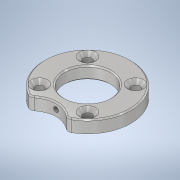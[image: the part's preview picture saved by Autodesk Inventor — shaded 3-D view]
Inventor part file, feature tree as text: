
AUTODESK INVENTOR PART (.ipt)
format: ipt  version: 2020.1 (Build 241239000, 239)  size: 221,696 bytes
history: native  units: mm
features: chamfer x3, fillet x2, sketch x2, projected_geometry x2, extrude x1, plane x1, hole x1, thread x1
ambient origin geometry x8: Origin, YZ Plane, XZ Plane, XY Plane, X Axis, Y Axis, Z Axis, Center Point
bodies: Solid1 (feature_tree)
feature tree (13):
  extrude  "Extrusion1"  Depth=3.5mm
  fillet  "Fillet1"  Radius=40.0mm
  fillet  "Fillet2"  [1 undecoded]
  chamfer  "Chamfer1"  Distance=15.0mm
  chamfer  "Chamfer2"  Distance=5.0mm
  chamfer  "Chamfer3"  Distance=2.0mm
  plane  "Work Plane1"
  hole  "Hole1"  [1 undecoded]
  thread  "Thread5"  [1 undecoded]
  sketch  "Sketch1"  dims[d0=18.5mm d2=3.5mm d4=40.0mm d6=360.0deg d8=45.0deg]
  sketch  "Sketch2"  dims[d10=19.0mm d11=15.0mm d12=5.0mm d13=0.0mm d14=2.0mm d15=1.0mm d24=0.5mm d25=2.0mm d26=45.0deg d27=0.0mm d30=8.0mm d32=0.5mm d33=2.0mm d34=45.0deg d36=27.5mm d37=1.5mm d38=2.0mm d39=45.0deg d40=2.5mm d41=5.0mm d42=2.5mm d43=2.0mm d44=6.0mm d45=4.0mm d46=2.0mm d47=90.0deg d48=8.0mm d49=0.0mm d50=3.516mm d51=0.0mm d52=0.0625mm d53=0.75mm d54=0.375mm]
  projected_geometry  "Projected Loop1"
  projected_geometry  "Projected Loop2"
note: 3 required parameter values undecoded (feature->parameter linkage not recoverable at this tier; creation-order binding heuristic only, values carry confidence <= 0.55)
